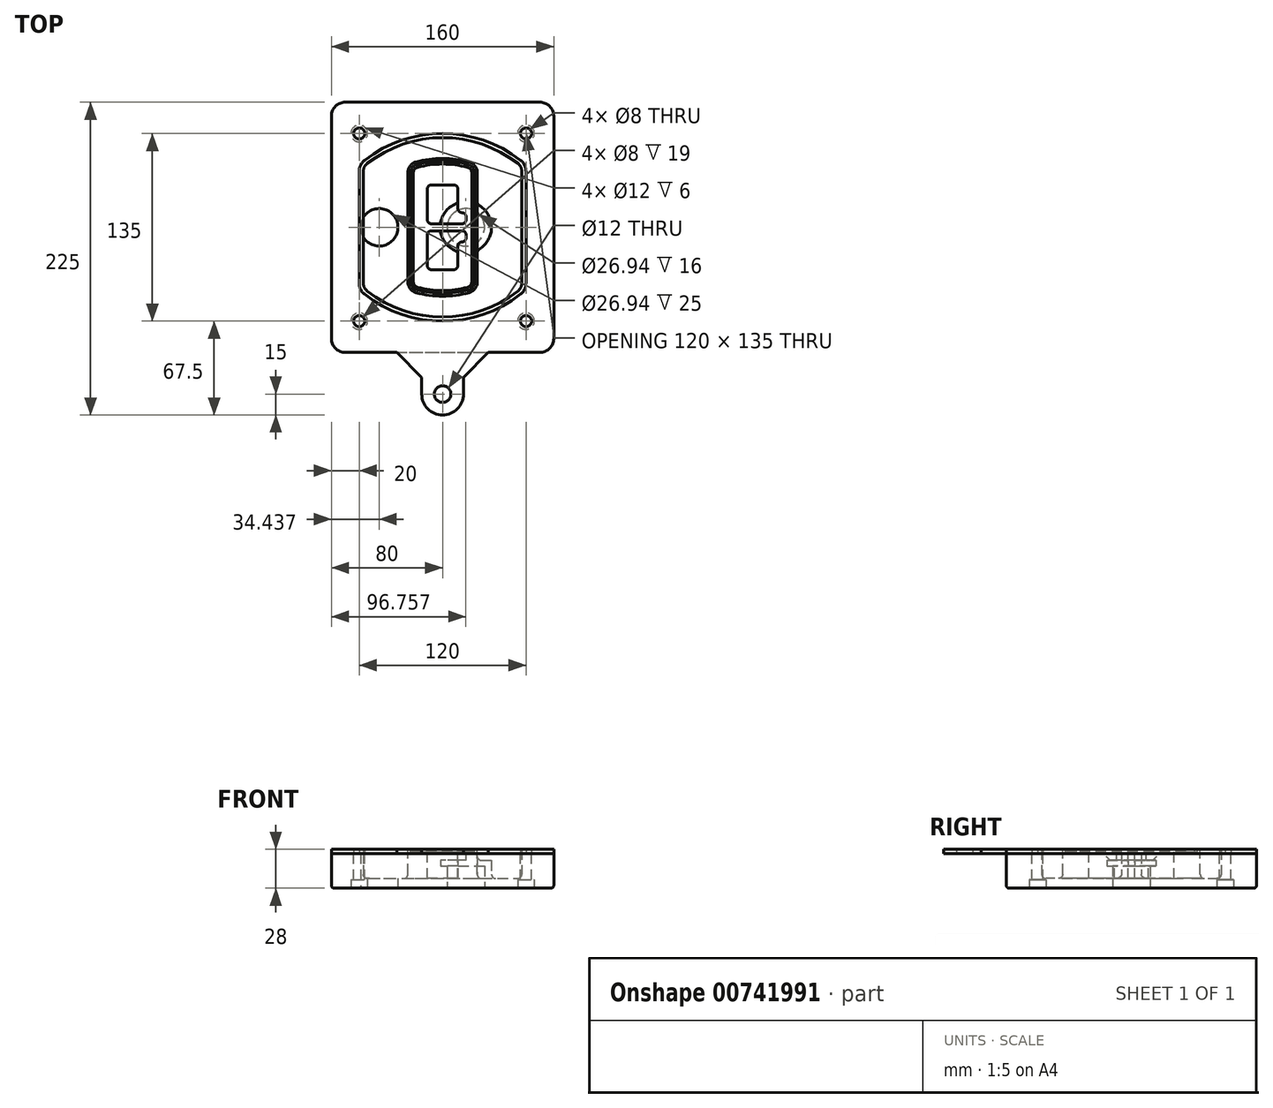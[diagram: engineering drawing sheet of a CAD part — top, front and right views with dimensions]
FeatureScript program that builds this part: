
annotation { "Feature Type Name" : "Feature", "Feature Type Description" : "" }
export const myFeature = defineFeature(function(context is Context, id is Id, definition is map)
    precondition{}
    {
        {
            var Q0;
            Q0=qCreatedBy(makeId("Top.planeOp"),FACE);
            var sketch = newSketch(context, id + "F0", { "sketchPlane" : qUnion([Q0])});
            skPoint(sketch, "E0.rect.middle", {"position": v(0, 0) * mm});
            skLineSegment(sketch, "E1.bottom", {"start": v(-70, -90) * mm, "end": v(70, -90) * mm});
            skLineSegment(sketch, "E1.top", {"start": v(-70, 90) * mm, "end": v(70, 90) * mm});
            skLineSegment(sketch, "E1.left", {"start": v(-80, -80) * mm, "end": v(-80, 80) * mm});
            skLineSegment(sketch, "E1.right", {"start": v(80, -80) * mm, "end": v(80, 80) * mm});
            skLineSegment(sketch, "E2", {"start": v(-80, 90) * mm, "end": v(80, -90) * mm, "construction": true});
            skLineSegment(sketch, "E3", {"start": v(80, 90) * mm, "end": v(-80, -90) * mm, "construction": true});
            skCircle(sketch, "E4", {"center": v(-60, 67.5) * mm, "radius": 4 * mm});
            skCircle(sketch, "E5", {"center": v(60, 67.5) * mm, "radius": 4 * mm});
            skCircle(sketch, "E6", {"center": v(60, -67.5) * mm, "radius": 4 * mm});
            skCircle(sketch, "E7", {"center": v(-60, -67.5) * mm, "radius": 4 * mm});
            skLineSegment(sketch, "E8", {"start": v(-60, 67.5) * mm, "end": v(60, 67.5) * mm, "construction": true});
            skLineSegment(sketch, "E9", {"start": v(60, 67.5) * mm, "end": v(60, -67.5) * mm, "construction": true});
            skLineSegment(sketch, "E10", {"start": v(60, -67.5) * mm, "end": v(-60, -67.5) * mm, "construction": true});
            skLineSegment(sketch, "E11", {"start": v(-60, -67.5) * mm, "end": v(-60, 67.5) * mm, "construction": true});
            skLineSegment(sketch, "E12", {"start": v(-60, 40.3) * mm, "end": v(-60, -40.3) * mm});
            skLineSegment(sketch, "E13", {"start": v(60, 40.3) * mm, "end": v(60, -40.3) * mm});
            skArc(sketch, "E14", {"start": v(56.15, 48.18) * mm, "mid": v(0, 67.5) * mm, "end": v(-56.15, 48.18) * mm});
            skArc(sketch, "E15", {"start": v(-56.15, -48.18) * mm, "mid": v(0, -67.5) * mm, "end": v(56.15, -48.18) * mm});
            skLineSegment(sketch, "E16", {"start": v(-60, 0) * mm, "end": v(60, 0) * mm, "construction": true});
            skPoint(sketch, "E17.visualSharp", {"position": v(-60, -45) * mm});
            skArc(sketch, "E17.filletArc", {"start": v(-60, -40.3) * mm, "mid": v(-58.99, -44.68) * mm, "end": v(-56.15, -48.18) * mm});
            skPoint(sketch, "E18.visualSharp", {"position": v(-60, 45) * mm});
            skArc(sketch, "E18.filletArc", {"start": v(-56.15, 48.18) * mm, "mid": v(-58.99, 44.68) * mm, "end": v(-60, 40.3) * mm});
            skPoint(sketch, "E19.visualSharp", {"position": v(60, 45) * mm});
            skArc(sketch, "E19.filletArc", {"start": v(60, 40.3) * mm, "mid": v(58.99, 44.68) * mm, "end": v(56.15, 48.18) * mm});
            skPoint(sketch, "E20.visualSharp", {"position": v(60, -45) * mm});
            skArc(sketch, "E20.filletArc", {"start": v(56.15, -48.18) * mm, "mid": v(58.99, -44.68) * mm, "end": v(60, -40.3) * mm});
            skPoint(sketch, "E21.visualSharp", {"position": v(-80, 90) * mm});
            skArc(sketch, "E21.filletArc", {"start": v(-70, 90) * mm, "mid": v(-77.07, 87.07) * mm, "end": v(-80, 80) * mm});
            skPoint(sketch, "E22.visualSharp", {"position": v(80, 90) * mm});
            skArc(sketch, "E22.filletArc", {"start": v(80, 80) * mm, "mid": v(77.07, 87.07) * mm, "end": v(70, 90) * mm});
            skPoint(sketch, "E23.visualSharp", {"position": v(80, -90) * mm});
            skArc(sketch, "E23.filletArc", {"start": v(70, -90) * mm, "mid": v(77.07, -87.07) * mm, "end": v(80, -80) * mm});
            skPoint(sketch, "E24.visualSharp", {"position": v(-80, -90) * mm});
            skArc(sketch, "E24.filletArc", {"start": v(-80, -80) * mm, "mid": v(-77.07, -87.07) * mm, "end": v(-70, -90) * mm});
            skArc(sketch, "E25.0", {"start": v(57, 40.3) * mm, "mid": v(56.3, 43.36) * mm, "end": v(54.3, 45.81) * mm});
            skLineSegment(sketch, "E25.1", {"start": v(57, 40.3) * mm, "end": v(57, -40.3) * mm});
            skArc(sketch, "E25.2", {"start": v(54.3, -45.81) * mm, "mid": v(56.3, -43.36) * mm, "end": v(57, -40.3) * mm});
            skArc(sketch, "E25.3", {"start": v(-54.3, -45.81) * mm, "mid": v(0, -64.5) * mm, "end": v(54.3, -45.81) * mm});
            skArc(sketch, "E25.4", {"start": v(-57, -40.3) * mm, "mid": v(-56.3, -43.36) * mm, "end": v(-54.3, -45.81) * mm});
            skArc(sketch, "E25.5", {"start": v(54.3, 45.81) * mm, "mid": v(0, 64.5) * mm, "end": v(-54.3, 45.81) * mm});
            skLineSegment(sketch, "E25.6", {"start": v(-57, 40.3) * mm, "end": v(-57, -40.3) * mm});
            skArc(sketch, "E25.7", {"start": v(-54.3, 45.81) * mm, "mid": v(-56.3, 43.36) * mm, "end": v(-57, 40.3) * mm});
            skArc(sketch, "E26.0", {"start": v(-58.62, 51.33) * mm, "mid": v(-62.58, 46.43) * mm, "end": v(-64, 40.3) * mm});
            skArc(sketch, "E26.1", {"start": v(58.62, 51.33) * mm, "mid": v(0, 71.5) * mm, "end": v(-58.62, 51.33) * mm});
            skArc(sketch, "E26.2", {"start": v(64, 40.3) * mm, "mid": v(62.58, 46.43) * mm, "end": v(58.62, 51.33) * mm});
            skLineSegment(sketch, "E26.3", {"start": v(64, 40.3) * mm, "end": v(64, -40.3) * mm});
            skArc(sketch, "E26.4", {"start": v(58.62, -51.33) * mm, "mid": v(62.58, -46.43) * mm, "end": v(64, -40.3) * mm});
            skLineSegment(sketch, "E26.5", {"start": v(-64, 40.3) * mm, "end": v(-64, -40.3) * mm});
            skArc(sketch, "E26.6", {"start": v(-58.62, -51.33) * mm, "mid": v(0, -71.5) * mm, "end": v(58.62, -51.33) * mm});
            skArc(sketch, "E26.7", {"start": v(-64, -40.3) * mm, "mid": v(-62.58, -46.43) * mm, "end": v(-58.62, -51.33) * mm});
            skSolve(sketch);
        }
        {
            var Q0;
            Q0=makeQuery(id+"F0.imprint","IMPRINT",FACE,{"disambiguationData":[TD([[makeQuery(id+"F0.imprint","IMPRINT",EDGE,{"derivedFrom":sQuery(id+"F0.wireOp",EDGE,"E1.bottom")}),1.0]])]});
            var Q1;
            Q1=makeQuery(id+"F0.imprint","IMPRINT",FACE,{"disambiguationData":[TD([[makeQuery(id+"F0.imprint","IMPRINT",EDGE,{"derivedFrom":sQuery(id+"F0.wireOp",EDGE,"E12")}),1.0]])]});
            var Q2;
            Q2=makeQuery(id+"F0.imprint","IMPRINT",FACE,{"disambiguationData":[TD([[makeQuery(id+"F0.imprint","IMPRINT",EDGE,{"derivedFrom":sQuery(id+"F0.wireOp",EDGE,"E25.0")}),1.0]])]});
            var Q3;
            Q3=makeQuery(id+"F0.imprint","IMPRINT",FACE,{"disambiguationData":[TD([[makeQuery(id+"F0.imprint","IMPRINT",EDGE,{"derivedFrom":sQuery(id+"F0.wireOp",EDGE,"E12")}),-1.0]])]});
            extrude(context, id + "F1", {"entities" : qUnion([Q0, Q1, Q2, Q3]), "oppositeDirection" : true, "depth" : 25 * mm});
        }
        {
            var Q0;
            Q0=makeQuery(id+"F0.imprint","IMPRINT",FACE,{"disambiguationData":[TD([[makeQuery(id+"F0.imprint","IMPRINT",EDGE,{"derivedFrom":sQuery(id+"F0.wireOp",EDGE,"E12")}),1.0]])]});
            extrude(context, id + "F2", {"entities" : qUnion([Q0]), "operationType" : NewBodyOperationType.ADD, "depth" : 3 * mm});
        }
        {
            var Q0;
            Q0=makeQuery(id+"F0.imprint","IMPRINT",FACE,{"disambiguationData":[TD([[makeQuery(id+"F0.imprint","IMPRINT",EDGE,{"derivedFrom":sQuery(id+"F0.wireOp",EDGE,"E25.0")}),1.0]])]});
            extrude(context, id + "F3", {"entities" : qUnion([Q0]), "operationType" : NewBodyOperationType.REMOVE, "oppositeDirection" : true, "depth" : 18 * mm});
        }
        {
            var Q0;
            Q0=makeQuery(id+"F2.opExtrude","CAP_FACE",FACE,{"disambiguationData":[OSD([sQuery(id+"F0.wireOp",EDGE,"E12"),sQuery(id+"F0.wireOp",EDGE,"E13"),sQuery(id+"F0.wireOp",EDGE,"E14"),sQuery(id+"F0.wireOp",EDGE,"E15"),sQuery(id+"F0.wireOp",EDGE,"E17.filletArc"),sQuery(id+"F0.wireOp",EDGE,"E18.filletArc"),sQuery(id+"F0.wireOp",EDGE,"E19.filletArc"),sQuery(id+"F0.wireOp",EDGE,"E20.filletArc"),sQuery(id+"F0.wireOp",EDGE,"E25.0"),sQuery(id+"F0.wireOp",EDGE,"E25.1"),sQuery(id+"F0.wireOp",EDGE,"E25.2"),sQuery(id+"F0.wireOp",EDGE,"E25.3"),sQuery(id+"F0.wireOp",EDGE,"E25.4"),sQuery(id+"F0.wireOp",EDGE,"E25.5"),sQuery(id+"F0.wireOp",EDGE,"E25.6"),sQuery(id+"F0.wireOp",EDGE,"E25.7")])],"isStart":false});
            var sketch = newSketch(context, id + "F4", { "sketchPlane" : qUnion([Q0])});
            skArc(sketch, "E27.0", {"start": v(-19.08, -46.97) * mm, "mid": v(0, -49.5) * mm, "end": v(19.08, -46.97) * mm});
            skArc(sketch, "E28.0", {"start": v(19.08, 46.97) * mm, "mid": v(0, 49.5) * mm, "end": v(-19.08, 46.97) * mm});
            skLineSegment(sketch, "E29", {"start": v(-25, 39.25) * mm, "end": v(-25, -39.25) * mm});
            skLineSegment(sketch, "E30", {"start": v(25, 39.25) * mm, "end": v(25, -39.25) * mm});
            skLineSegment(sketch, "E31", {"start": v(-25, 45.1) * mm, "end": v(25, 45.1) * mm, "construction": true});
            skLineSegment(sketch, "E32", {"start": v(-25, -45.1) * mm, "end": v(25, -45.1) * mm, "construction": true});
            skPoint(sketch, "E33.visualSharp", {"position": v(-25, 45.1) * mm});
            skArc(sketch, "E33.filletArc", {"start": v(-19.08, 46.97) * mm, "mid": v(-23.35, 44.11) * mm, "end": v(-25, 39.25) * mm});
            skPoint(sketch, "E34.visualSharp", {"position": v(25, 45.1) * mm});
            skArc(sketch, "E34.filletArc", {"start": v(25, 39.25) * mm, "mid": v(23.35, 44.11) * mm, "end": v(19.08, 46.97) * mm});
            skPoint(sketch, "E35.visualSharp", {"position": v(25, -45.1) * mm});
            skArc(sketch, "E35.filletArc", {"start": v(19.08, -46.97) * mm, "mid": v(23.35, -44.11) * mm, "end": v(25, -39.25) * mm});
            skPoint(sketch, "E36.visualSharp", {"position": v(-25, -45.1) * mm});
            skArc(sketch, "E36.filletArc", {"start": v(-25, -39.25) * mm, "mid": v(-23.35, -44.11) * mm, "end": v(-19.08, -46.97) * mm});
            skArc(sketch, "E37.0", {"start": v(54.3, 45.81) * mm, "mid": v(0, 64.5) * mm, "end": v(-54.3, 45.81) * mm});
            skArc(sketch, "E37.1", {"start": v(-54.3, 45.81) * mm, "mid": v(-56.3, 43.36) * mm, "end": v(-57, 40.3) * mm});
            skLineSegment(sketch, "E37.2", {"start": v(-57, 40.3) * mm, "end": v(-57, -40.3) * mm});
            skArc(sketch, "E37.3", {"start": v(-57, -40.3) * mm, "mid": v(-56.3, -43.36) * mm, "end": v(-54.3, -45.81) * mm});
            skArc(sketch, "E37.4", {"start": v(-54.3, -45.81) * mm, "mid": v(0, -64.5) * mm, "end": v(54.3, -45.81) * mm});
            skArc(sketch, "E37.5", {"start": v(54.3, -45.81) * mm, "mid": v(56.3, -43.36) * mm, "end": v(57, -40.3) * mm});
            skLineSegment(sketch, "E37.6", {"start": v(57, 40.3) * mm, "end": v(57, -40.3) * mm});
            skArc(sketch, "E37.7", {"start": v(57, 40.3) * mm, "mid": v(56.3, 43.36) * mm, "end": v(54.3, 45.81) * mm});
            skLineSegment(sketch, "E38.0", {"start": v(23, 39.25) * mm, "end": v(23, -39.25) * mm});
            skArc(sketch, "E38.1", {"start": v(18.56, -45.04) * mm, "mid": v(21.76, -42.9) * mm, "end": v(23, -39.25) * mm});
            skArc(sketch, "E38.2", {"start": v(-18.56, -45.04) * mm, "mid": v(0, -47.5) * mm, "end": v(18.56, -45.04) * mm});
            skArc(sketch, "E38.3", {"start": v(-23, -39.25) * mm, "mid": v(-21.76, -42.9) * mm, "end": v(-18.56, -45.04) * mm});
            skLineSegment(sketch, "E38.4", {"start": v(-23, 39.25) * mm, "end": v(-23, -39.25) * mm});
            skArc(sketch, "E38.5", {"start": v(23, 39.25) * mm, "mid": v(21.76, 42.9) * mm, "end": v(18.56, 45.04) * mm});
            skArc(sketch, "E38.6", {"start": v(-18.56, 45.04) * mm, "mid": v(-21.76, 42.9) * mm, "end": v(-23, 39.25) * mm});
            skArc(sketch, "E38.7", {"start": v(18.56, 45.04) * mm, "mid": v(0, 47.5) * mm, "end": v(-18.56, 45.04) * mm});
            skArc(sketch, "E39.0", {"start": v(21, 39.25) * mm, "mid": v(20.18, 41.68) * mm, "end": v(18.04, 43.1) * mm});
            skLineSegment(sketch, "E39.1", {"start": v(21, 39.25) * mm, "end": v(21, -39.25) * mm});
            skArc(sketch, "E39.2", {"start": v(18.04, -43.1) * mm, "mid": v(20.18, -41.68) * mm, "end": v(21, -39.25) * mm});
            skArc(sketch, "E39.3", {"start": v(-18.04, -43.1) * mm, "mid": v(0, -45.5) * mm, "end": v(18.04, -43.1) * mm});
            skArc(sketch, "E39.4", {"start": v(-21, -39.25) * mm, "mid": v(-20.18, -41.68) * mm, "end": v(-18.04, -43.1) * mm});
            skArc(sketch, "E39.5", {"start": v(18.04, 43.1) * mm, "mid": v(0, 45.5) * mm, "end": v(-18.04, 43.1) * mm});
            skLineSegment(sketch, "E39.6", {"start": v(-21, 39.25) * mm, "end": v(-21, -39.25) * mm});
            skArc(sketch, "E39.7", {"start": v(-18.04, 43.1) * mm, "mid": v(-20.18, 41.68) * mm, "end": v(-21, 39.25) * mm});
            skLineSegment(sketch, "E40", {"start": v(-25, 0) * mm, "end": v(25, 0) * mm, "construction": true});
            skLineSegment(sketch, "E41", {"start": v(-11, 5.5) * mm, "end": v(-11, 27.5) * mm});
            skLineSegment(sketch, "E42", {"start": v(-8, 30.5) * mm, "end": v(8, 30.5) * mm});
            skLineSegment(sketch, "E43", {"start": v(11, 27.5) * mm, "end": v(11, 13.5) * mm});
            skLineSegment(sketch, "E44", {"start": v(14, 10.5) * mm, "end": v(14, 10.5) * mm});
            skLineSegment(sketch, "E45", {"start": v(17, 7.5) * mm, "end": v(17, 5.5) * mm});
            skLineSegment(sketch, "E46", {"start": v(14, 2.5) * mm, "end": v(-8, 2.5) * mm});
            skPoint(sketch, "E47.visualSharp", {"position": v(-11, 30.5) * mm});
            skArc(sketch, "E47.filletArc", {"start": v(-8, 30.5) * mm, "mid": v(-10.12, 29.62) * mm, "end": v(-11, 27.5) * mm});
            skPoint(sketch, "E48.visualSharp", {"position": v(11, 30.5) * mm});
            skArc(sketch, "E48.filletArc", {"start": v(11, 27.5) * mm, "mid": v(10.12, 29.62) * mm, "end": v(8, 30.5) * mm});
            skPoint(sketch, "E49.visualSharp", {"position": v(11, 10.5) * mm});
            skArc(sketch, "E49.filletArc", {"start": v(11, 13.5) * mm, "mid": v(11.88, 11.38) * mm, "end": v(14, 10.5) * mm});
            skPoint(sketch, "E50.visualSharp", {"position": v(17, 10.5) * mm});
            skArc(sketch, "E50.filletArc", {"start": v(17, 7.5) * mm, "mid": v(16.12, 9.62) * mm, "end": v(14, 10.5) * mm});
            skPoint(sketch, "E51.visualSharp", {"position": v(17, 2.5) * mm});
            skArc(sketch, "E51.filletArc", {"start": v(14, 2.5) * mm, "mid": v(16.12, 3.38) * mm, "end": v(17, 5.5) * mm});
            skPoint(sketch, "E52.visualSharp", {"position": v(-11, 2.5) * mm});
            skArc(sketch, "E52.filletArc", {"start": v(-11, 5.5) * mm, "mid": v(-10.12, 3.38) * mm, "end": v(-8, 2.5) * mm});
            skLineSegment(sketch, "E53.0.MirrorCS", {"start": v(14, -2.5) * mm, "end": v(-8, -2.5) * mm});
            skArc(sketch, "E54.0.MirrorCS", {"start": v(-11, -5.5) * mm, "mid": v(-10.12, -3.38) * mm, "end": v(-8, -2.5) * mm});
            skLineSegment(sketch, "E55.0.MirrorCS", {"start": v(-11, -5.5) * mm, "end": v(-11, -27.5) * mm});
            skArc(sketch, "E56.0.MirrorCS", {"start": v(-8, -30.5) * mm, "mid": v(-10.12, -29.62) * mm, "end": v(-11, -27.5) * mm});
            skLineSegment(sketch, "E57.0.MirrorCS", {"start": v(-8, -30.5) * mm, "end": v(8, -30.5) * mm});
            skArc(sketch, "E58.0.MirrorCS", {"start": v(11, -27.5) * mm, "mid": v(10.12, -29.62) * mm, "end": v(8, -30.5) * mm});
            skLineSegment(sketch, "E59.0.MirrorCS", {"start": v(11, -27.5) * mm, "end": v(11, -13.5) * mm});
            skArc(sketch, "E60.0.MirrorCS", {"start": v(11, -13.5) * mm, "mid": v(11.88, -11.38) * mm, "end": v(14, -10.5) * mm});
            skArc(sketch, "E61.0.MirrorCS", {"start": v(17, -7.5) * mm, "mid": v(16.12, -9.62) * mm, "end": v(14, -10.5) * mm});
            skLineSegment(sketch, "E62.0.MirrorCS", {"start": v(17, -7.5) * mm, "end": v(17, -5.5) * mm});
            skArc(sketch, "E63.0.MirrorCS", {"start": v(14, -2.5) * mm, "mid": v(16.12, -3.38) * mm, "end": v(17, -5.5) * mm});
            skSolve(sketch);
        }
        {
            var Q0;
            Q0=makeQuery(id+"F4.imprint","IMPRINT",FACE,{"disambiguationData":[TD([[makeQuery(id+"F4.imprint","IMPRINT",EDGE,{"derivedFrom":sQuery(id+"F4.wireOp",EDGE,"E27.0")}),1.0]])]});
            var Q1;
            Q1=makeQuery(id+"F4.imprint","IMPRINT",FACE,{"disambiguationData":[TD([[makeQuery(id+"F4.imprint","IMPRINT",EDGE,{"derivedFrom":sQuery(id+"F4.wireOp",EDGE,"E38.0")}),-1.0]])]});
            var Q2;
            Q2=makeQuery(id+"F4.imprint","IMPRINT",FACE,{"disambiguationData":[TD([[makeQuery(id+"F4.imprint","IMPRINT",EDGE,{"derivedFrom":sQuery(id+"F4.wireOp",EDGE,"E39.0")}),1.0]])]});
            extrude(context, id + "F5", {"entities" : qUnion([Q0, Q1, Q2]), "operationType" : NewBodyOperationType.ADD, "endBound" : BoundingType.UP_TO_NEXT, "oppositeDirection" : true, "depth" : 25 * mm});
        }
        {
            var Q0;
            Q0=makeQuery(id+"F4.imprint","IMPRINT",FACE,{"disambiguationData":[TD([[makeQuery(id+"F4.imprint","IMPRINT",EDGE,{"derivedFrom":sQuery(id+"F4.wireOp",EDGE,"E38.0")}),-1.0]])]});
            extrude(context, id + "F6", {"entities" : qUnion([Q0]), "operationType" : NewBodyOperationType.REMOVE, "oppositeDirection" : true, "depth" : 2 * mm});
        }
        {
            var Q0;
            Q0=makeQuery(id+"F1.opExtrude","CAP_FACE",FACE,{"disambiguationData":[OSD([sQuery(id+"F0.wireOp",EDGE,"E1.bottom"),sQuery(id+"F0.wireOp",EDGE,"E1.top"),sQuery(id+"F0.wireOp",EDGE,"E1.left"),sQuery(id+"F0.wireOp",EDGE,"E1.right"),sQuery(id+"F0.wireOp",EDGE,"E4"),sQuery(id+"F0.wireOp",EDGE,"E5"),sQuery(id+"F0.wireOp",EDGE,"E6"),sQuery(id+"F0.wireOp",EDGE,"E7"),sQuery(id+"F0.wireOp",EDGE,"E21.filletArc"),sQuery(id+"F0.wireOp",EDGE,"E22.filletArc"),sQuery(id+"F0.wireOp",EDGE,"E23.filletArc"),sQuery(id+"F0.wireOp",EDGE,"E24.filletArc")])],"isStart":false});
            var sketch = newSketch(context, id + "F7", { "sketchPlane" : qUnion([Q0])});
            skCircle(sketch, "E64", {"center": v(16.76, 0) * mm, "radius": 13.47 * mm});
            skCircle(sketch, "E65", {"center": v(-45.56, 0) * mm, "radius": 13.47 * mm});
            skLineSegment(sketch, "E66", {"start": v(80, 0) * mm, "end": v(-80, 0) * mm});
            skCircle(sketch, "E67", {"center": v(16.76, 0) * mm, "radius": 18.47 * mm});
            skCircle(sketch, "E68", {"center": v(60, -67.5) * mm, "radius": 6 * mm});
            skCircle(sketch, "E69", {"center": v(-60, -67.5) * mm, "radius": 6 * mm});
            skCircle(sketch, "E70", {"center": v(-60, 67.5) * mm, "radius": 6 * mm});
            skCircle(sketch, "E71", {"center": v(60, 67.5) * mm, "radius": 6 * mm});
            skSolve(sketch);
        }
        {
            var Q0;
            {var subQ1=sQuery(id+"F7.wireOp",EDGE,"E66");var subQ4=sQuery(id+"F7.wireOp",EDGE,"E64");var subQ6=makeQuery(id+"F7.imprint","INTERSECT",VERTEX,{"disambiguationData":[OD(0.0)],"derivedFrom":[subQ4,subQ1]});Q0=makeQuery(id+"F7.imprint","IMPRINT",FACE,{"disambiguationData":[TD([[makeQuery(id+"F7.imprint","IMPRINT",EDGE,{"disambiguationData":[TD([[subQ6,-1.0]])],"derivedFrom":subQ4}),-1.0]])]});}
            var Q1;
            {var subQ0=sQuery(id+"F7.wireOp",EDGE,"E66");var subQ1=sQuery(id+"F7.wireOp",EDGE,"E64");var subQ3=makeQuery(id+"F7.imprint","INTERSECT",VERTEX,{"disambiguationData":[OD(0.0)],"derivedFrom":[subQ1,subQ0]});Q1=makeQuery(id+"F7.imprint","IMPRINT",FACE,{"disambiguationData":[TD([[makeQuery(id+"F7.imprint","IMPRINT",EDGE,{"disambiguationData":[TD([[subQ3,-1.0]])],"derivedFrom":subQ1}),1.0]])]});}
            var Q2;
            {var subQ0=sQuery(id+"F7.wireOp",EDGE,"E66");var subQ1=sQuery(id+"F7.wireOp",EDGE,"E64");var subQ3=makeQuery(id+"F7.imprint","INTERSECT",VERTEX,{"disambiguationData":[OD(0.0)],"derivedFrom":[subQ1,subQ0]});Q2=makeQuery(id+"F7.imprint","IMPRINT",FACE,{"disambiguationData":[TD([[makeQuery(id+"F7.imprint","IMPRINT",EDGE,{"disambiguationData":[TD([[subQ3,1.0]])],"derivedFrom":subQ1}),1.0]])]});}
            var Q3;
            {var subQ1=sQuery(id+"F7.wireOp",EDGE,"E66");var subQ4=sQuery(id+"F7.wireOp",EDGE,"E64");var subQ6=makeQuery(id+"F7.imprint","INTERSECT",VERTEX,{"disambiguationData":[OD(0.0)],"derivedFrom":[subQ4,subQ1]});Q3=makeQuery(id+"F7.imprint","IMPRINT",FACE,{"disambiguationData":[TD([[makeQuery(id+"F7.imprint","IMPRINT",EDGE,{"disambiguationData":[TD([[subQ6,1.0]])],"derivedFrom":subQ4}),-1.0]])]});}
            extrude(context, id + "F8", {"entities" : qUnion([Q0, Q1, Q2, Q3]), "operationType" : NewBodyOperationType.ADD, "oppositeDirection" : true, "depth" : 20 * mm});
        }
        {
            var Q0;
            {var subQ0=sQuery(id+"F7.wireOp",EDGE,"E66");var subQ1=sQuery(id+"F7.wireOp",EDGE,"E64");var subQ3=makeQuery(id+"F7.imprint","INTERSECT",VERTEX,{"disambiguationData":[OD(0.0)],"derivedFrom":[subQ1,subQ0]});Q0=makeQuery(id+"F7.imprint","IMPRINT",FACE,{"disambiguationData":[TD([[makeQuery(id+"F7.imprint","IMPRINT",EDGE,{"disambiguationData":[TD([[subQ3,-1.0]])],"derivedFrom":subQ1}),1.0]])]});}
            var Q1;
            {var subQ0=sQuery(id+"F7.wireOp",EDGE,"E66");var subQ1=sQuery(id+"F7.wireOp",EDGE,"E64");var subQ3=makeQuery(id+"F7.imprint","INTERSECT",VERTEX,{"disambiguationData":[OD(0.0)],"derivedFrom":[subQ1,subQ0]});Q1=makeQuery(id+"F7.imprint","IMPRINT",FACE,{"disambiguationData":[TD([[makeQuery(id+"F7.imprint","IMPRINT",EDGE,{"disambiguationData":[TD([[subQ3,1.0]])],"derivedFrom":subQ1}),1.0]])]});}
            extrude(context, id + "F9", {"entities" : qUnion([Q0, Q1]), "operationType" : NewBodyOperationType.REMOVE, "oppositeDirection" : true, "depth" : 16 * mm});
        }
        {
            var Q0;
            {var subQ0=sQuery(id+"F7.wireOp",EDGE,"E66");var subQ1=sQuery(id+"F7.wireOp",EDGE,"E65");var subQ3=makeQuery(id+"F7.imprint","INTERSECT",VERTEX,{"disambiguationData":[OD(0.0)],"derivedFrom":[subQ1,subQ0]});Q0=makeQuery(id+"F7.imprint","IMPRINT",FACE,{"disambiguationData":[TD([[makeQuery(id+"F7.imprint","IMPRINT",EDGE,{"disambiguationData":[TD([[subQ3,-1.0]])],"derivedFrom":subQ1}),1.0]])]});}
            var Q1;
            {var subQ0=sQuery(id+"F7.wireOp",EDGE,"E66");var subQ1=sQuery(id+"F7.wireOp",EDGE,"E65");var subQ3=makeQuery(id+"F7.imprint","INTERSECT",VERTEX,{"disambiguationData":[OD(0.0)],"derivedFrom":[subQ1,subQ0]});Q1=makeQuery(id+"F7.imprint","IMPRINT",FACE,{"disambiguationData":[TD([[makeQuery(id+"F7.imprint","IMPRINT",EDGE,{"disambiguationData":[TD([[subQ3,1.0]])],"derivedFrom":subQ1}),1.0]])]});}
            extrude(context, id + "F10", {"entities" : qUnion([Q0, Q1]), "operationType" : NewBodyOperationType.REMOVE, "oppositeDirection" : true, "depth" : 25 * mm});
        }
        {
            var Q0;
            Q0=makeQuery(id+"F7.imprint","IMPRINT",FACE,{"disambiguationData":[TD([[makeQuery(id+"F7.imprint","IMPRINT",EDGE,{"derivedFrom":sQuery(id+"F7.wireOp",EDGE,"E68")}),1.0]])]});
            var Q1;
            Q1=makeQuery(id+"F7.imprint","IMPRINT",FACE,{"disambiguationData":[TD([[makeQuery(id+"F7.imprint","IMPRINT",EDGE,{"derivedFrom":makeQuery(id+"F1.opExtrude","CAP_EDGE",EDGE,{"disambiguationData":[OSD([sQuery(id+"F0.wireOp",EDGE,"E5")])],"isStart":false})}),-1.0]])]});
            var Q2;
            Q2=makeQuery(id+"F7.imprint","IMPRINT",FACE,{"disambiguationData":[TD([[makeQuery(id+"F7.imprint","IMPRINT",EDGE,{"derivedFrom":sQuery(id+"F7.wireOp",EDGE,"E69")}),1.0]])]});
            var Q3;
            Q3=makeQuery(id+"F7.imprint","IMPRINT",FACE,{"disambiguationData":[TD([[makeQuery(id+"F7.imprint","IMPRINT",EDGE,{"derivedFrom":makeQuery(id+"F1.opExtrude","CAP_EDGE",EDGE,{"disambiguationData":[OSD([sQuery(id+"F0.wireOp",EDGE,"E4")])],"isStart":false})}),-1.0]])]});
            var Q4;
            Q4=makeQuery(id+"F7.imprint","IMPRINT",FACE,{"disambiguationData":[TD([[makeQuery(id+"F7.imprint","IMPRINT",EDGE,{"derivedFrom":sQuery(id+"F7.wireOp",EDGE,"E70")}),1.0]])]});
            var Q5;
            Q5=makeQuery(id+"F7.imprint","IMPRINT",FACE,{"disambiguationData":[TD([[makeQuery(id+"F7.imprint","IMPRINT",EDGE,{"derivedFrom":makeQuery(id+"F1.opExtrude","CAP_EDGE",EDGE,{"disambiguationData":[OSD([sQuery(id+"F0.wireOp",EDGE,"E7")])],"isStart":false})}),-1.0]])]});
            var Q6;
            Q6=makeQuery(id+"F7.imprint","IMPRINT",FACE,{"disambiguationData":[TD([[makeQuery(id+"F7.imprint","IMPRINT",EDGE,{"derivedFrom":sQuery(id+"F7.wireOp",EDGE,"E71")}),1.0]])]});
            var Q7;
            Q7=makeQuery(id+"F7.imprint","IMPRINT",FACE,{"disambiguationData":[TD([[makeQuery(id+"F7.imprint","IMPRINT",EDGE,{"derivedFrom":makeQuery(id+"F1.opExtrude","CAP_EDGE",EDGE,{"disambiguationData":[OSD([sQuery(id+"F0.wireOp",EDGE,"E6")])],"isStart":false})}),-1.0]])]});
            var Q8;
            Q8 = qSketchRegion(id + "F16", true);
            extrude(context, id + "F11", {"entities" : qUnion([Q0, Q1, Q2, Q3, Q4, Q5, Q6, Q7, Q8]), "operationType" : NewBodyOperationType.REMOVE, "oppositeDirection" : true, "depth" : 6 * mm, "offsetDistance" : 25 * mm});
        }
        {
            var Q0;
            Q0=makeQuery(id+"F9.boolean.opBoolean","COPY",FACE,{"derivedFrom":makeQuery(id+"F9.opExtrude","CAP_FACE",FACE,{"disambiguationData":[OSD([sQuery(id+"F7.wireOp",EDGE,"E64")])],"isStart":false})});
            var sketch = newSketch(context, id + "F12", { "sketchPlane" : qUnion([Q0])});
            skArc(sketch, "E72.0", {"start": v(11, 17.55) * mm, "mid": v(2.57, 11.82) * mm, "end": v(-1.54, 2.5) * mm});
            skArc(sketch, "E72.1", {"start": v(-1.54, -2.5) * mm, "mid": v(2.57, -11.82) * mm, "end": v(11, -17.55) * mm});
            skLineSegment(sketch, "E73", {"start": v(-1.54, -2.5) * mm, "end": v(14, -2.5) * mm});
            skLineSegment(sketch, "E74.0", {"start": v(14, 2.5) * mm, "end": v(-1.54, 2.5) * mm});
            skArc(sketch, "E74.1", {"start": v(14, 2.5) * mm, "mid": v(16.12, 3.38) * mm, "end": v(17, 5.5) * mm});
            skLineSegment(sketch, "E74.2", {"start": v(17, 7.5) * mm, "end": v(17, 5.5) * mm});
            skArc(sketch, "E74.3", {"start": v(17, 7.5) * mm, "mid": v(16.12, 9.62) * mm, "end": v(14, 10.5) * mm});
            skArc(sketch, "E74.4", {"start": v(11, 13.5) * mm, "mid": v(11.88, 11.38) * mm, "end": v(14, 10.5) * mm});
            skLineSegment(sketch, "E74.5", {"start": v(11, 17.55) * mm, "end": v(11, 13.5) * mm});
            skLineSegment(sketch, "E74.7", {"start": v(14, -2.5) * mm, "end": v(-1.54, -2.5) * mm});
            skArc(sketch, "E74.8", {"start": v(14, -2.5) * mm, "mid": v(16.12, -3.38) * mm, "end": v(17, -5.5) * mm});
            skLineSegment(sketch, "E74.9", {"start": v(17, -7.5) * mm, "end": v(17, -5.5) * mm});
            skArc(sketch, "E74.10", {"start": v(17, -7.5) * mm, "mid": v(16.12, -9.62) * mm, "end": v(14, -10.5) * mm});
            skArc(sketch, "E74.11", {"start": v(11, -13.5) * mm, "mid": v(11.88, -11.38) * mm, "end": v(14, -10.5) * mm});
            skLineSegment(sketch, "E74.12", {"start": v(11, -17.55) * mm, "end": v(11, -13.5) * mm});
            skPoint(sketch, "E75.orphan", {"position": v(11, -27.5) * mm});
            skPoint(sketch, "E76.orphan", {"position": v(-8, -2.5) * mm});
            skPoint(sketch, "E77.orphan", {"position": v(-8, 2.5) * mm});
            skPoint(sketch, "E78.orphan", {"position": v(11, 27.5) * mm});
            skSolve(sketch);
        }
        {
            var Q0;
            {var subQ7=sQuery(id+"F12.wireOp",EDGE,"E72.0");var subQ14=sQuery(id+"F12.wireOp",EDGE,"E72.1");var subQ16=sQuery(id+"F12.wireOp",EDGE,"E74.1");var subQ18=sQuery(id+"F12.wireOp",EDGE,"E74.8");Q0=qUnion([makeQuery(id+"F12.imprint","IMPRINT",FACE,{"disambiguationData":[TD([[makeQuery(id+"F12.imprint","IMPRINT",EDGE,{"derivedFrom":subQ7}),1.0]])]}),makeQuery(id+"F12.imprint","IMPRINT",FACE,{"disambiguationData":[TD([[makeQuery(id+"F12.imprint","IMPRINT",EDGE,{"derivedFrom":subQ14}),1.0]])]}),makeQuery(id+"F12.imprint","IMPRINT",FACE,{"disambiguationData":[TD([[makeQuery(id+"F12.imprint","IMPRINT",EDGE,{"derivedFrom":subQ16}),1.0]])]}),makeQuery(id+"F12.imprint","IMPRINT",FACE,{"disambiguationData":[TD([[makeQuery(id+"F12.imprint","IMPRINT",EDGE,{"derivedFrom":subQ18}),-1.0]])]})]);}
            var Q1;
            Q1=makeQuery(id+"F5.boolean.opBoolean","SPLIT",FACE,{"disambiguationData":[TD([makeQuery(id+"F5.opExtrude","SWEPT_FACE",FACE,{"disambiguationData":[OSD([sQuery(id+"F4.wireOp",EDGE,"E41")])]})])],"derivedFrom":makeQuery(id+"F3.boolean.opBoolean","COPY",FACE,{"derivedFrom":makeQuery(id+"F3.opExtrude","CAP_FACE",FACE,{"disambiguationData":[OSD([sQuery(id+"F0.wireOp",EDGE,"E25.0"),sQuery(id+"F0.wireOp",EDGE,"E25.1"),sQuery(id+"F0.wireOp",EDGE,"E25.2"),sQuery(id+"F0.wireOp",EDGE,"E25.3"),sQuery(id+"F0.wireOp",EDGE,"E25.4"),sQuery(id+"F0.wireOp",EDGE,"E25.5"),sQuery(id+"F0.wireOp",EDGE,"E25.6"),sQuery(id+"F0.wireOp",EDGE,"E25.7")])],"isStart":false})})});
            extrude(context, id + "F13", {"entities" : qUnion([Q0]), "operationType" : NewBodyOperationType.REMOVE, "endBound" : BoundingType.UP_TO_SURFACE, "endBoundEntityFace" : qUnion([Q1]), "depth" : 25 * mm, "offsetDistance" : 25 * mm});
        }
        {
            var Q0;
            Q0=makeQuery(id+"F3.boolean.opBoolean","COPY",EDGE,{"derivedFrom":makeQuery(id+"F3.opExtrude","CAP_EDGE",EDGE,{"disambiguationData":[OSD([sQuery(id+"F0.wireOp",EDGE,"E25.6")])],"isStart":false})});
            var Q1;
            Q1=makeQuery(id+"F8.boolean.opBoolean","INTERSECT",EDGE,{"derivedFrom":[makeQuery(id+"F5.opExtrude","SWEPT_FACE",FACE,{"disambiguationData":[OSD([sQuery(id+"F4.wireOp",EDGE,"E30")])]}),makeQuery(id+"F8.opExtrude","CAP_FACE",FACE,{"disambiguationData":[OSD([sQuery(id+"F7.wireOp",EDGE,"E67")])],"isStart":false})]});
            var Q2;
            Q2=makeQuery(id+"F8.boolean.opBoolean","INTERSECT",EDGE,{"disambiguationData":[OD(1.0)],"derivedFrom":[makeQuery(id+"F5.opExtrude","SWEPT_FACE",FACE,{"disambiguationData":[OSD([sQuery(id+"F4.wireOp",EDGE,"E30")])]}),makeQuery(id+"F8.opExtrude","SWEPT_FACE",FACE,{"disambiguationData":[OSD([sQuery(id+"F7.wireOp",EDGE,"E67")])]})]});
            var Q3;
            {var subQ0=sQuery(id+"F4.wireOp",EDGE,"E30");Q3=makeQuery(id+"F8.boolean.opBoolean","SPLIT",EDGE,{"disambiguationData":[TD([makeQuery(id+"F5.opExtrude","SWEPT_FACE",FACE,{"disambiguationData":[OSD([sQuery(id+"F4.wireOp",EDGE,"E35.filletArc")])]})])],"derivedFrom":makeQuery(id+"F5.opExtrude","CAP_EDGE",EDGE,{"disambiguationData":[OSD([subQ0])],"isStart":false})});}
            var Q4;
            {var subQ0=sQuery(id+"F0.wireOp",EDGE,"E25.7");var subQ1=sQuery(id+"F0.wireOp",EDGE,"E25.1");var subQ2=sQuery(id+"F0.wireOp",EDGE,"E25.6");var subQ3=sQuery(id+"F0.wireOp",EDGE,"E25.5");var subQ4=sQuery(id+"F0.wireOp",EDGE,"E25.4");var subQ5=sQuery(id+"F0.wireOp",EDGE,"E25.0");var subQ6=sQuery(id+"F0.wireOp",EDGE,"E25.2");var subQ7=sQuery(id+"F0.wireOp",EDGE,"E25.3");Q4=makeQuery(id+"F8.boolean.opBoolean","INTERSECT",EDGE,{"derivedFrom":[makeQuery(id+"F5.boolean.opBoolean","SPLIT",FACE,{"disambiguationData":[TD([makeQuery(id+"F2.opExtrude","SWEPT_FACE",FACE,{"disambiguationData":[OSD([subQ5])]})])],"derivedFrom":makeQuery(id+"F3.boolean.opBoolean","COPY",FACE,{"derivedFrom":makeQuery(id+"F3.opExtrude","CAP_FACE",FACE,{"disambiguationData":[OSD([subQ5,subQ1,subQ6,subQ7,subQ4,subQ3,subQ2,subQ0])],"isStart":false})})}),makeQuery(id+"F8.opExtrude","SWEPT_FACE",FACE,{"disambiguationData":[OSD([sQuery(id+"F7.wireOp",EDGE,"E67")])]})]});}
            var Q5;
            Q5=makeQuery(id+"F8.boolean.opBoolean","INTERSECT",EDGE,{"disambiguationData":[OD(0.0)],"derivedFrom":[makeQuery(id+"F5.opExtrude","SWEPT_FACE",FACE,{"disambiguationData":[OSD([sQuery(id+"F4.wireOp",EDGE,"E30")])]}),makeQuery(id+"F8.opExtrude","SWEPT_FACE",FACE,{"disambiguationData":[OSD([sQuery(id+"F7.wireOp",EDGE,"E67")])]})]});
            fillet(context, id + "F14", {"entities" : qUnion([Q0, Q1, Q2, Q3, Q4, Q5]), "radius" : 3 * mm, "tangentPropagation" : true, "allowEdgeOverflow" : false});
        }
        {
            var Q0;
            Q0=makeQuery(id+"F1.opExtrude","CAP_EDGE",EDGE,{"disambiguationData":[OSD([sQuery(id+"F0.wireOp",EDGE,"E1.bottom")])],"isStart":false});
            fillet(context, id + "F15", {"entities" : qUnion([Q0]), "radius" : 2 * mm, "tangentPropagation" : true, "allowEdgeOverflow" : false});
        }
        {
            var Q0;
            {var subQ0=sQuery(id+"F0.wireOp",EDGE,"E21.filletArc");var subQ1=sQuery(id+"F0.wireOp",EDGE,"E7");var subQ2=sQuery(id+"F0.wireOp",EDGE,"E6");var subQ3=sQuery(id+"F0.wireOp",EDGE,"E5");var subQ4=sQuery(id+"F0.wireOp",EDGE,"E4");var subQ5=sQuery(id+"F0.wireOp",EDGE,"E22.filletArc");var subQ6=sQuery(id+"F0.wireOp",EDGE,"E1.bottom");var subQ7=sQuery(id+"F0.wireOp",EDGE,"E1.right");var subQ8=sQuery(id+"F0.wireOp",EDGE,"E1.top");var subQ9=sQuery(id+"F0.wireOp",EDGE,"E1.left");var subQ10=sQuery(id+"F0.wireOp",EDGE,"E23.filletArc");var subQ11=sQuery(id+"F0.wireOp",EDGE,"E24.filletArc");Q0=makeQuery(id+"F2.boolean.opBoolean","SPLIT",FACE,{"disambiguationData":[TD([makeQuery(id+"F1.opExtrude","SWEPT_FACE",FACE,{"disambiguationData":[OSD([subQ6])]})])],"derivedFrom":makeQuery(id+"F1.opExtrude","CAP_FACE",FACE,{"disambiguationData":[OSD([subQ6,subQ8,subQ9,subQ7,subQ4,subQ3,subQ2,subQ1,subQ0,subQ5,subQ10,subQ11])],"isStart":true})});}
            var sketch = newSketch(context, id + "F16", { "sketchPlane" : qUnion([Q0])});
            skLineSegment(sketch, "E79.0", {"start": v(-70, 90) * mm, "end": v(70, 90) * mm});
            skArc(sketch, "E79.1", {"start": v(-70, 90) * mm, "mid": v(-77.07, 87.07) * mm, "end": v(-80, 80) * mm});
            skLineSegment(sketch, "E79.2", {"start": v(-80, -80) * mm, "end": v(-80, 80) * mm});
            skArc(sketch, "E79.3", {"start": v(-80, -80) * mm, "mid": v(-77.07, -87.07) * mm, "end": v(-70, -90) * mm});
            skLineSegment(sketch, "E79.4", {"start": v(-70, -90) * mm, "end": v(70, -90) * mm});
            skArc(sketch, "E79.5", {"start": v(70, -90) * mm, "mid": v(77.07, -87.07) * mm, "end": v(80, -80) * mm});
            skLineSegment(sketch, "E79.6", {"start": v(80, -80) * mm, "end": v(80, 80) * mm});
            skArc(sketch, "E79.7", {"start": v(80, 80) * mm, "mid": v(77.07, 87.07) * mm, "end": v(70, 90) * mm});
            skCircle(sketch, "E79.8", {"center": v(60, 67.5) * mm, "radius": 4 * mm});
            skCircle(sketch, "E79.9", {"center": v(-60, 67.5) * mm, "radius": 4 * mm});
            skCircle(sketch, "E79.10", {"center": v(-60, -67.5) * mm, "radius": 4 * mm});
            skCircle(sketch, "E79.11", {"center": v(60, -67.5) * mm, "radius": 4 * mm});
            skArc(sketch, "E79.12", {"start": v(-56.15, -48.18) * mm, "mid": v(0, -67.5) * mm, "end": v(56.15, -48.18) * mm});
            skArc(sketch, "E79.13", {"start": v(56.15, -48.18) * mm, "mid": v(58.99, -44.68) * mm, "end": v(60, -40.3) * mm});
            skLineSegment(sketch, "E79.14", {"start": v(60, 40.3) * mm, "end": v(60, -40.3) * mm});
            skArc(sketch, "E79.15", {"start": v(60, 40.3) * mm, "mid": v(58.99, 44.68) * mm, "end": v(56.15, 48.18) * mm});
            skArc(sketch, "E79.16", {"start": v(56.15, 48.18) * mm, "mid": v(0, 67.5) * mm, "end": v(-56.15, 48.18) * mm});
            skArc(sketch, "E79.17", {"start": v(-56.15, 48.18) * mm, "mid": v(-58.99, 44.68) * mm, "end": v(-60, 40.3) * mm});
            skLineSegment(sketch, "E79.18", {"start": v(-60, 40.3) * mm, "end": v(-60, -40.3) * mm});
            skArc(sketch, "E79.19", {"start": v(-60, -40.3) * mm, "mid": v(-58.99, -44.68) * mm, "end": v(-56.15, -48.18) * mm});
            skLineSegment(sketch, "E80.0.0", {"start": v(70, 90) * mm, "end": v(-70, 90) * mm});
            skLineSegment(sketch, "E80.0.2", {"start": v(-80, 80) * mm, "end": v(-80, -80) * mm});
            skLineSegment(sketch, "E81", {"start": v(0, 90) * mm, "end": v(0, 120) * mm, "construction": true});
            skCircle(sketch, "E82", {"center": v(0, 120) * mm, "radius": 6 * mm});
            skLineSegment(sketch, "E83", {"start": v(-33, 90) * mm, "end": v(-15, 108) * mm});
            skLineSegment(sketch, "E84", {"start": v(15, 108) * mm, "end": v(33, 90) * mm});
            skLineSegment(sketch, "E85", {"start": v(-15, 120) * mm, "end": v(-15, 108) * mm});
            skLineSegment(sketch, "E86", {"start": v(15, 108) * mm, "end": v(15, 120) * mm});
            skArc(sketch, "E87", {"start": v(15, 120) * mm, "mid": v(0, 135) * mm, "end": v(-15, 120) * mm});
            skLineSegment(sketch, "E88", {"start": v(0, -90) * mm, "end": v(0, -120) * mm, "construction": true});
            skLineSegment(sketch, "E89.MirrorCS", {"start": v(33, 90) * mm, "end": v(15, 108) * mm});
            skLineSegment(sketch, "E90.MirrorCS", {"start": v(-15, 108) * mm, "end": v(-33, 90) * mm});
            skLineSegment(sketch, "E91.MirrorCS", {"start": v(-15, 108) * mm, "end": v(-15, 120) * mm});
            skArc(sketch, "E92.MirrorCS", {"start": v(-15, 120) * mm, "mid": v(0, 135) * mm, "end": v(15, 120) * mm});
            skLineSegment(sketch, "E93.MirrorCS", {"start": v(15, 120) * mm, "end": v(15, 108) * mm});
            skLineSegment(sketch, "E94.MirrorCS", {"start": v(70, -90) * mm, "end": v(-70, -90) * mm});
            skLineSegment(sketch, "E95.MirrorCS", {"start": v(15, -288) * mm, "end": v(33, -270) * mm});
            skLineSegment(sketch, "E96.MirrorCS", {"start": v(-15, -288) * mm, "end": v(-33, -270) * mm});
            skLineSegment(sketch, "E97.MirrorCS", {"start": v(-70, -270) * mm, "end": v(70, -270) * mm});
            skLineSegment(sketch, "E98", {"start": v(-80, 0) * mm, "end": v(80, 0) * mm, "construction": true});
            skLineSegment(sketch, "E99.MirrorCS", {"start": v(-15, -108) * mm, "end": v(-15, -120) * mm});
            skLineSegment(sketch, "E100.MirrorCS", {"start": v(-33, -90) * mm, "end": v(-15, -108) * mm});
            skLineSegment(sketch, "E101.MirrorCS", {"start": v(15, -108) * mm, "end": v(33, -90) * mm});
            skLineSegment(sketch, "E102.MirrorCS", {"start": v(15, -120) * mm, "end": v(15, -108) * mm});
            skArc(sketch, "E103.MirrorCS", {"start": v(-15, -120) * mm, "mid": v(0, -135) * mm, "end": v(15, -120) * mm});
            skCircle(sketch, "E104.MirrorC", {"center": v(0, -120) * mm, "radius": 6 * mm});
            skSolve(sketch);
        }
        {
            var Q0;
            Q0=makeQuery(id+"F16.imprint","IMPRINT",FACE,{"disambiguationData":[TD([[makeQuery(id+"F16.imprint","IMPRINT",EDGE,{"derivedFrom":sQuery(id+"F16.wireOp",EDGE,"E79.8")}),-1.0]])]});
            var Q1;
            Q1=makeQuery(id+"F16.imprint","IMPRINT",FACE,{"disambiguationData":[TD([[makeQuery(id+"F16.imprint","IMPRINT",EDGE,{"derivedFrom":sQuery(id+"F16.wireOp",EDGE,"E99.MirrorCS")}),1.0]])]});
            var Q2;
            Q2=makeQuery(id+"F16.imprint","IMPRINT",FACE,{"disambiguationData":[TD([[makeQuery(id+"F16.imprint","IMPRINT",EDGE,{"derivedFrom":sQuery(id+"F16.wireOp",EDGE,"E91.MirrorCS")}),-1.0]])]});
            var Q3;
            Q3=makeQuery(id+"F2.opExtrude","CAP_FACE",FACE,{"disambiguationData":[OSD([sQuery(id+"F0.wireOp",EDGE,"E12"),sQuery(id+"F0.wireOp",EDGE,"E13"),sQuery(id+"F0.wireOp",EDGE,"E14"),sQuery(id+"F0.wireOp",EDGE,"E15"),sQuery(id+"F0.wireOp",EDGE,"E17.filletArc"),sQuery(id+"F0.wireOp",EDGE,"E18.filletArc"),sQuery(id+"F0.wireOp",EDGE,"E19.filletArc"),sQuery(id+"F0.wireOp",EDGE,"E20.filletArc"),sQuery(id+"F0.wireOp",EDGE,"E25.0"),sQuery(id+"F0.wireOp",EDGE,"E25.1"),sQuery(id+"F0.wireOp",EDGE,"E25.2"),sQuery(id+"F0.wireOp",EDGE,"E25.3"),sQuery(id+"F0.wireOp",EDGE,"E25.4"),sQuery(id+"F0.wireOp",EDGE,"E25.5"),sQuery(id+"F0.wireOp",EDGE,"E25.6"),sQuery(id+"F0.wireOp",EDGE,"E25.7")])],"isStart":false});
            extrude(context, id + "F17", {"entities" : qUnion([Q0, Q1, Q2]), "endBound" : BoundingType.UP_TO_SURFACE, "depth" : 25 * mm, "endBoundEntityFace" : qUnion([Q3]), "offsetDistance" : 25 * mm});
        }
    });
